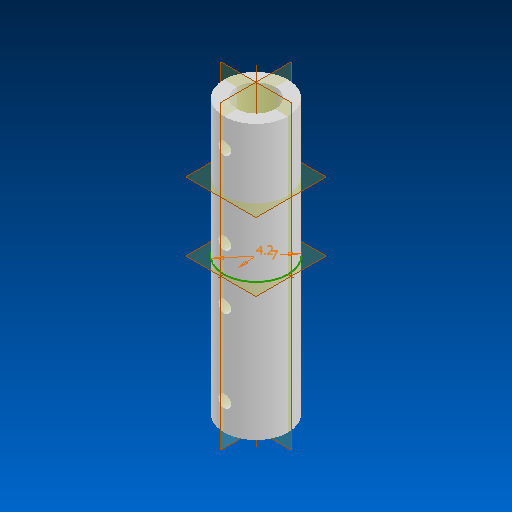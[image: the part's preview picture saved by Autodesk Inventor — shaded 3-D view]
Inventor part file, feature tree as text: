
AUTODESK INVENTOR PART (.ipt)
format: ipt  version: 2025 (Build 290162000, 162)  size: 272,384 bytes
history: native  units: mm
features: mirror x3, sketch x2, extrude x1, hole x1, plane x1
ambient origin geometry x8: Origin, YZ Plane, XZ Plane, XY Plane, X Axis, Y Axis, Z Axis, Center Point
bodies: Solid1 (feature_tree)
feature tree (8):
  extrude  "Extrusion1"  Depth=7.0mm
  hole  "Hole1"  [1 undecoded]
  plane  "Work Plane1"
  mirror  "Mirror1"
  mirror  "Mirror2"
  mirror  "Mirror3"
  sketch  "Sketch1"  dims[d0=4.2mm d1=7.0mm]
  sketch  "Sketch2"  dims[d2=15.0mm d3=0.0mm d4=1.4mm d5=6.0mm d6=3.023mm d7=2.0mm d8=14.3117mm d9=4.8mm d10=20.594885mm]
note: 1 required parameter value undecoded (feature->parameter linkage not recoverable at this tier; creation-order binding heuristic only, values carry confidence <= 0.55)
